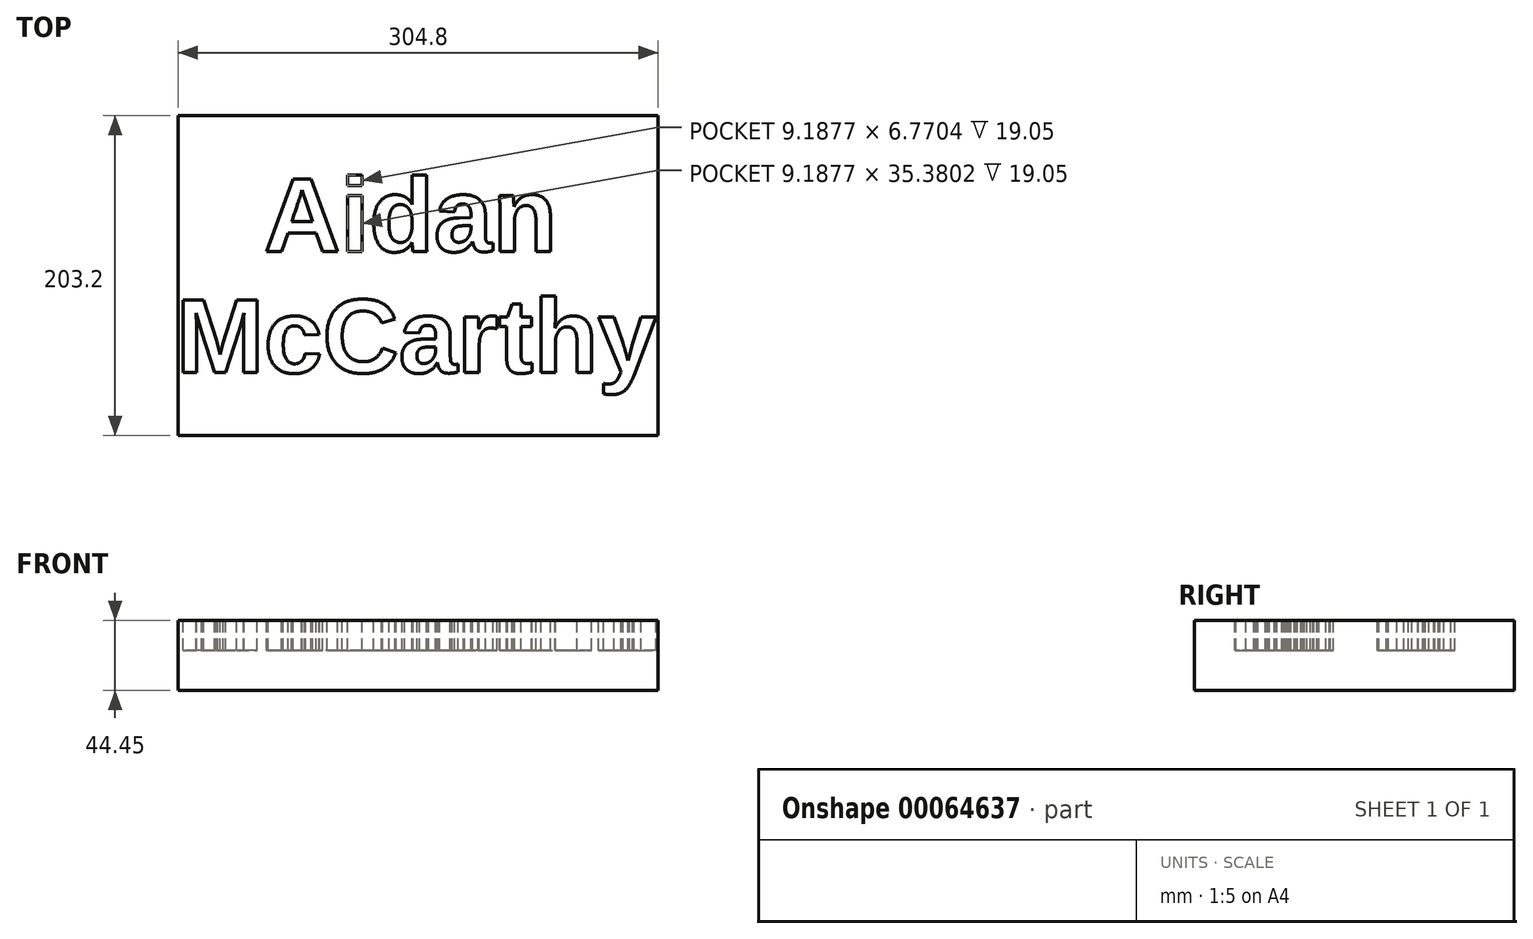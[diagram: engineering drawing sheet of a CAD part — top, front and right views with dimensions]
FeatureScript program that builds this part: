
annotation { "Feature Type Name" : "Feature", "Feature Type Description" : "" }
export const myFeature = defineFeature(function(context is Context, id is Id, definition is map)
    precondition{}
    {
        {
            var Q0;
            Q0=qCreatedBy(makeId("Top.planeOp"),FACE);
            var sketch = newSketch(context, id + "F0", { "sketchPlane" : qUnion([Q0])});
            skLineSegment(sketch, "E0.bottom", {"start": v(0, 0) * mm, "end": v(-304.8, 0) * mm});
            skLineSegment(sketch, "E0.top", {"start": v(0, 203.2) * mm, "end": v(-304.8, 203.2) * mm});
            skLineSegment(sketch, "E0.left", {"start": v(0, 0) * mm, "end": v(0, 203.2) * mm});
            skLineSegment(sketch, "E0.right", {"start": v(-304.8, 0) * mm, "end": v(-304.8, 203.2) * mm});
            skSolve(sketch);
        }
        {
            var Q0;
            Q0=makeQuery(id+"F0.imprint","IMPRINT",FACE,{"disambiguationData":[TD([[makeQuery(id+"F0.imprint","IMPRINT",EDGE,{"derivedFrom":sQuery(id+"F0.wireOp",EDGE,"E0.bottom")}),-1.0]])]});
            extrude(context, id + "F1", {"entities" : qUnion([Q0]), "depth" : 44.45 * mm});
        }
        {
            var Q0;
            Q0=makeQuery(id+"F1.opExtrude","CAP_FACE",FACE,{"disambiguationData":[OSD([sQuery(id+"F0.wireOp",EDGE,"E0.bottom"),sQuery(id+"F0.wireOp",EDGE,"E0.top"),sQuery(id+"F0.wireOp",EDGE,"E0.left"),sQuery(id+"F0.wireOp",EDGE,"E0.right")])],"isStart":false});
            var sketch = newSketch(context, id + "F2", { "sketchPlane" : qUnion([Q0])});
            skText(sketch, "E1", { "text": "   Aidan\nMcCarthy", "fontName": "Arimo-Bold.ttf"});
            const initialGuessF2  = {"E1": [-0.30602, 0.11688, 1, 0, 0.04822]};
            skSetInitialGuess(sketch, initialGuessF2);
            skSolve(sketch);
        }
        {
            var Q0;
            Q0 = qSketchRegion(id + "F2", true);
            extrude(context, id + "F3", {"entities" : qUnion([Q0]), "operationType" : NewBodyOperationType.REMOVE, "oppositeDirection" : true, "depth" : 19.05 * mm});
        }
    });
